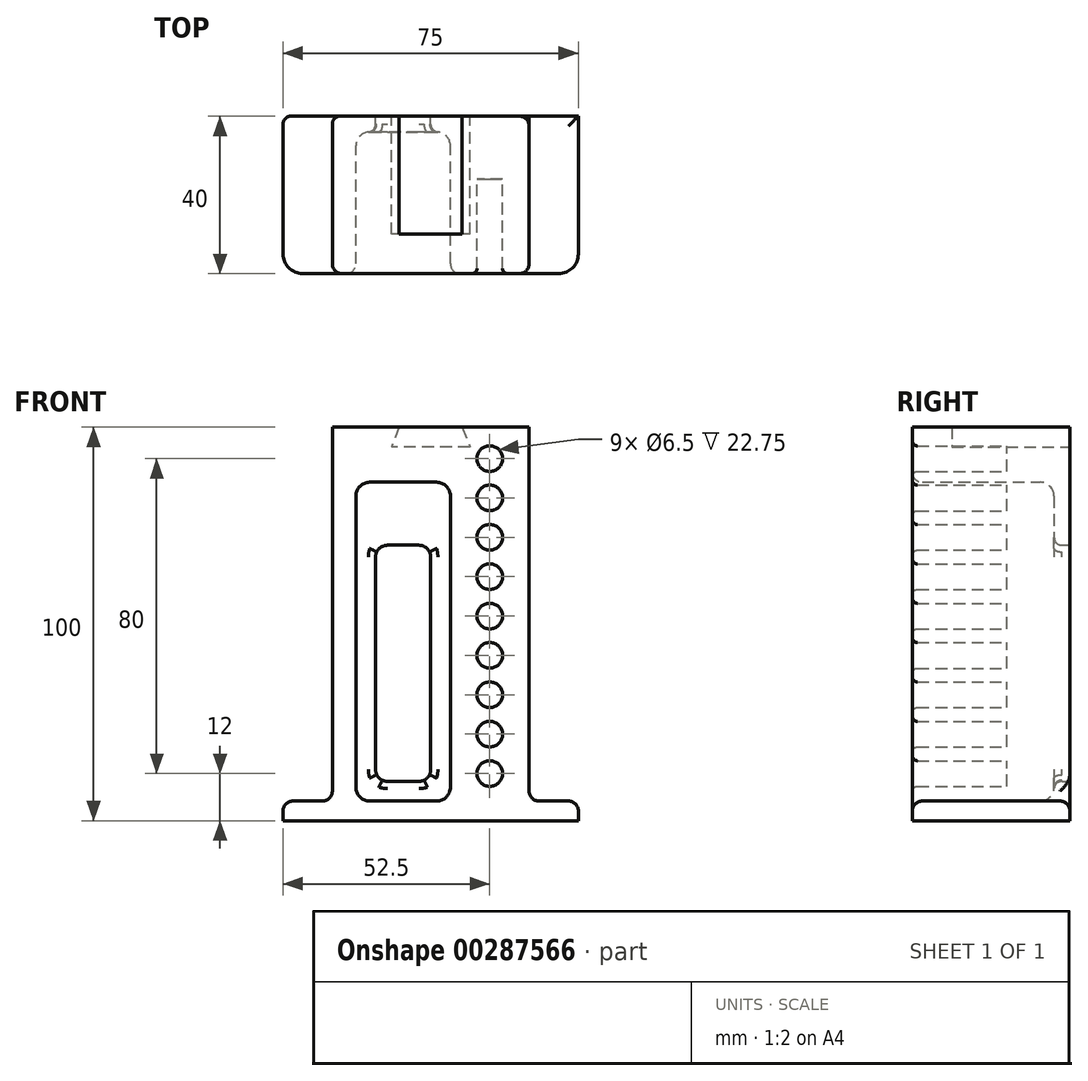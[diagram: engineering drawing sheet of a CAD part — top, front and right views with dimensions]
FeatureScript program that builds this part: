
annotation { "Feature Type Name" : "Feature", "Feature Type Description" : "" }
export const myFeature = defineFeature(function(context is Context, id is Id, definition is map)
    precondition{}
    {
        {
            var Q0;
            Q0=qCreatedBy(makeId("Front.planeOp"),FACE);
            var sketch = newSketch(context, id + "F0", { "sketchPlane" : qUnion([Q0])});
            skLineSegment(sketch, "E0", {"start": v(0, 0) * mm, "end": v(-25, 0) * mm});
            skLineSegment(sketch, "E1", {"start": v(-25, 0) * mm, "end": v(-25, -26.82) * mm});
            skLineSegment(sketch, "E2.bottom", {"start": v(-25, 0) * mm, "end": v(25, 0) * mm});
            skLineSegment(sketch, "E2.top", {"start": v(-25, 100) * mm, "end": v(25, 100) * mm});
            skLineSegment(sketch, "E2.left", {"start": v(-25, 0) * mm, "end": v(-25, 100) * mm});
            skLineSegment(sketch, "E2.right", {"start": v(25, 0) * mm, "end": v(25, 100) * mm});
            skSolve(sketch);
        }
        {
            var Q0;
            Q0=qSketchRegion(id+"F0",true);
            extrude(context, id + "F1", {"entities" : qUnion([Q0]), "endBound" : BoundingType.SYMMETRIC, "depth" : 40 * mm});
        }
        {
            var Q0;
            Q0=qCreatedBy(makeId("Top.planeOp"),FACE);
            var sketch = newSketch(context, id + "F2", { "sketchPlane" : qUnion([Q0])});
            skLineSegment(sketch, "E3.bottom", {"start": v(37.5, -20) * mm, "end": v(-37.5, -20) * mm});
            skLineSegment(sketch, "E3.top", {"start": v(37.5, 20) * mm, "end": v(-37.5, 20) * mm});
            skLineSegment(sketch, "E3.left", {"start": v(37.5, -20) * mm, "end": v(37.5, 20) * mm});
            skLineSegment(sketch, "E3.right", {"start": v(-37.5, -20) * mm, "end": v(-37.5, 20) * mm});
            skPoint(sketch, "E3.middle", {"position": v(0, 0) * mm});
            skSolve(sketch);
        }
        {
            var Q0;
            Q0=qSketchRegion(id+"F2",true);
            extrude(context, id + "F3", {"entities" : qUnion([Q0]), "operationType" : NewBodyOperationType.ADD, "depth" : 5 * mm});
        }
        {
            var Q0;
            Q0=qCreatedBy(makeId("Front.planeOp"),FACE);
            var sketch = newSketch(context, id + "F4", { "sketchPlane" : qUnion([Q0])});
            skLineSegment(sketch, "E4", {"start": v(0, 0) * mm, "end": v(0, 5) * mm});
            skLineSegment(sketch, "E5", {"start": v(0, 5) * mm, "end": v(-19, 5) * mm});
            skLineSegment(sketch, "E6", {"start": v(-19, 5) * mm, "end": v(-19, 86) * mm});
            skLineSegment(sketch, "E7", {"start": v(-19, 86) * mm, "end": v(5, 86) * mm});
            skLineSegment(sketch, "E8", {"start": v(5, 86) * mm, "end": v(5, 5) * mm});
            skLineSegment(sketch, "E9", {"start": v(5, 5) * mm, "end": v(0, 5) * mm});
            skSolve(sketch);
        }
        {
            var Q0;
            Q0=qSketchRegion(id+"F4",true);
            extrude(context, id + "F5", {"entities" : qUnion([Q0]), "endBound" : BoundingType.SYMMETRIC, "depth" : 48 * mm});
        }
        {
            var Q0;
            Q0=makeQuery(id+"F5.opExtrude","SWEPT_EDGE",EDGE,{"disambiguationData":[OSD([sQuery(id+"F4.wireOp",EDGE,"E6"),sQuery(id+"F4.wireOp",EDGE,"E7")])]});
            var Q1;
            Q1=makeQuery(id+"F5.opExtrude","SWEPT_EDGE",EDGE,{"disambiguationData":[OSD([sQuery(id+"F4.wireOp",EDGE,"E7"),sQuery(id+"F4.wireOp",EDGE,"E8")])]});
            var Q2;
            Q2=makeQuery(id+"F5.opExtrude","SWEPT_EDGE",EDGE,{"disambiguationData":[OSD([sQuery(id+"F4.wireOp",EDGE,"E5"),sQuery(id+"F4.wireOp",EDGE,"E6")])]});
            var Q3;
            Q3=makeQuery(id+"F5.opExtrude","SWEPT_EDGE",EDGE,{"disambiguationData":[OSD([sQuery(id+"F4.wireOp",EDGE,"E8"),sQuery(id+"F4.wireOp",EDGE,"E9")])]});
            var Q4;
            Q4=makeQuery(id+"F5.opExtrude","CAP_EDGE",EDGE,{"disambiguationData":[OSD([sQuery(id+"F4.wireOp",EDGE,"E7")])],"isStart":true});
            var Q5;
            Q5=makeQuery(id+"F5.opExtrude","CAP_EDGE",EDGE,{"disambiguationData":[OSD([sQuery(id+"F4.wireOp",EDGE,"E8")])],"isStart":true});
            var Q6;
            Q6=makeQuery(id+"F5.opExtrude","CAP_EDGE",EDGE,{"disambiguationData":[OSD([sQuery(id+"F4.wireOp",EDGE,"E6")])],"isStart":true});
            var Q7;
            Q7=makeQuery(id+"F5.opExtrude","CAP_EDGE",EDGE,{"disambiguationData":[OSD([sQuery(id+"F4.wireOp",EDGE,"E5"),sQuery(id+"F4.wireOp",EDGE,"E9")])],"isStart":true});
            fillet(context, id + "F6", {"entities" : qUnion([Q0, Q1, Q2, Q3, Q4, Q5, Q6, Q7]), "radius" : 3.5 * mm, "tangentPropagation" : true, "allowEdgeOverflow" : false});
        }
        {
            var Q0;
            Q0=makeQuery(id+"F5.opExtrude","SWEPT_BODY",BODY,{"disambiguationData":[OSD([sQuery(id+"F4.wireOp",EDGE,"E5"),sQuery(id+"F4.wireOp",EDGE,"E6"),sQuery(id+"F4.wireOp",EDGE,"E7"),sQuery(id+"F4.wireOp",EDGE,"E8"),sQuery(id+"F4.wireOp",EDGE,"E9")])]});
            transform(context, id + "F7", {"entities" : qUnion([Q0]), "transformType" : TransformType.TRANSLATION_3D, "dx" : 0 * mm, "dy" : -8 * mm, "dz" : 0 * mm, "makeCopy" : false});
        }
        {
            var Q0;
            Q0=makeQuery(id+"F5.opExtrude","SWEPT_BODY",BODY,{"disambiguationData":[OSD([sQuery(id+"F4.wireOp",EDGE,"E5"),sQuery(id+"F4.wireOp",EDGE,"E6"),sQuery(id+"F4.wireOp",EDGE,"E7"),sQuery(id+"F4.wireOp",EDGE,"E8"),sQuery(id+"F4.wireOp",EDGE,"E9")])]});
            transform(context, id + "F8", {"entities" : qUnion([Q0]), "transformType" : TransformType.COPY});
        }
        {
            var Q0;
            Q0=makeQuery(id+"F8.opPattern","COPY",BODY,{"derivedFrom":makeQuery(id+"F5.opExtrude","SWEPT_BODY",BODY,{"disambiguationData":[OSD([sQuery(id+"F4.wireOp",EDGE,"E5"),sQuery(id+"F4.wireOp",EDGE,"E6"),sQuery(id+"F4.wireOp",EDGE,"E7"),sQuery(id+"F4.wireOp",EDGE,"E8"),sQuery(id+"F4.wireOp",EDGE,"E9")])]}),"instanceName":"1"});
            var Q1;
            Q1=makeQuery(id+"F1.opExtrude","SWEPT_BODY",BODY,{"disambiguationData":[OSD([sQuery(id+"F0.wireOp",EDGE,"E2.bottom"),sQuery(id+"F0.wireOp",EDGE,"E2.top"),sQuery(id+"F0.wireOp",EDGE,"E2.left"),sQuery(id+"F0.wireOp",EDGE,"E2.right")])]});
            booleanBodies(context, id + "F9", {"operationType" : BooleanOperationType.SUBTRACTION, "tools" : qUnion([Q0]), "targets" : qUnion([Q1])});
        }
        {
            var Q0;
            {var subQ0=sQuery(id+"F2.wireOp",EDGE,"E3.bottom");var subQ2=sQuery(id+"F0.wireOp",EDGE,"E2.right");Q0=makeQuery(id+"F3.boolean.opBoolean","SPLIT",EDGE,{"disambiguationData":[TD([makeQuery(id+"F1.opExtrude","SWEPT_FACE",FACE,{"disambiguationData":[OSD([subQ2])]})])],"derivedFrom":makeQuery(id+"F3.opExtrude","CAP_EDGE",EDGE,{"disambiguationData":[OSD([subQ0])],"isStart":false})});}
            var Q1;
            Q1=makeQuery(id+"F3.opExtrude","CAP_EDGE",EDGE,{"disambiguationData":[OSD([sQuery(id+"F2.wireOp",EDGE,"E3.left")])],"isStart":false});
            var Q2;
            Q2=makeQuery(id+"F1.opExtrude","CAP_EDGE",EDGE,{"disambiguationData":[OSD([sQuery(id+"F0.wireOp",EDGE,"E2.right")])],"isStart":false});
            var Q3;
            {var subQ1=sQuery(id+"F2.wireOp",EDGE,"E3.top");var subQ2=sQuery(id+"F0.wireOp",EDGE,"E2.right");Q3=makeQuery(id+"F3.boolean.opBoolean","SPLIT",EDGE,{"disambiguationData":[TD([makeQuery(id+"F1.opExtrude","SWEPT_FACE",FACE,{"disambiguationData":[OSD([subQ2])]})])],"derivedFrom":makeQuery(id+"F3.opExtrude","CAP_EDGE",EDGE,{"disambiguationData":[OSD([subQ1])],"isStart":false})});}
            var Q4;
            {var subQ1=sQuery(id+"F2.wireOp",EDGE,"E3.bottom");var subQ2=sQuery(id+"F0.wireOp",EDGE,"E2.left");Q4=makeQuery(id+"F3.boolean.opBoolean","SPLIT",EDGE,{"disambiguationData":[TD([makeQuery(id+"F1.opExtrude","SWEPT_FACE",FACE,{"disambiguationData":[OSD([subQ2])]})])],"derivedFrom":makeQuery(id+"F3.opExtrude","CAP_EDGE",EDGE,{"disambiguationData":[OSD([subQ1])],"isStart":false})});}
            var Q5;
            Q5=makeQuery(id+"F3.opExtrude","CAP_EDGE",EDGE,{"disambiguationData":[OSD([sQuery(id+"F2.wireOp",EDGE,"E3.right")])],"isStart":false});
            var Q6;
            Q6=makeQuery(id+"F9.opBoolean","INTERSECT",EDGE,{"derivedFrom":[makeQuery(id+"F3.boolean.opBoolean","MERGE",FACE,{"derivedFrom":[makeQuery(id+"F1.opExtrude","CAP_FACE",FACE,{"disambiguationData":[OSD([sQuery(id+"F0.wireOp",EDGE,"E2.bottom"),sQuery(id+"F0.wireOp",EDGE,"E2.top"),sQuery(id+"F0.wireOp",EDGE,"E2.left"),sQuery(id+"F0.wireOp",EDGE,"E2.right")])],"isStart":false}),makeQuery(id+"F3.opExtrude","SWEPT_FACE",FACE,{"disambiguationData":[OSD([sQuery(id+"F2.wireOp",EDGE,"E3.bottom")])]})]}),makeQuery(id+"F8.opPattern","COPY",FACE,{"derivedFrom":makeQuery(id+"F5.opExtrude","SWEPT_FACE",FACE,{"disambiguationData":[OSD([sQuery(id+"F4.wireOp",EDGE,"E6")])]}),"instanceName":"1"})]});
            var Q7;
            Q7=makeQuery(id+"F1.opExtrude","CAP_EDGE",EDGE,{"disambiguationData":[OSD([sQuery(id+"F0.wireOp",EDGE,"E2.left")])],"isStart":false});
            var Q8;
            Q8=makeQuery(id+"F3.boolean.opBoolean","INTERSECT",EDGE,{"derivedFrom":[makeQuery(id+"F1.opExtrude","SWEPT_FACE",FACE,{"disambiguationData":[OSD([sQuery(id+"F0.wireOp",EDGE,"E2.left")])]}),makeQuery(id+"F3.opExtrude","CAP_FACE",FACE,{"disambiguationData":[OSD([sQuery(id+"F2.wireOp",EDGE,"E3.bottom"),sQuery(id+"F2.wireOp",EDGE,"E3.top"),sQuery(id+"F2.wireOp",EDGE,"E3.left"),sQuery(id+"F2.wireOp",EDGE,"E3.right")])],"isStart":false})]});
            var Q9;
            Q9=makeQuery(id+"F3.boolean.opBoolean","INTERSECT",EDGE,{"derivedFrom":[makeQuery(id+"F1.opExtrude","SWEPT_FACE",FACE,{"disambiguationData":[OSD([sQuery(id+"F0.wireOp",EDGE,"E2.right")])]}),makeQuery(id+"F3.opExtrude","CAP_FACE",FACE,{"disambiguationData":[OSD([sQuery(id+"F2.wireOp",EDGE,"E3.bottom"),sQuery(id+"F2.wireOp",EDGE,"E3.top"),sQuery(id+"F2.wireOp",EDGE,"E3.left"),sQuery(id+"F2.wireOp",EDGE,"E3.right")])],"isStart":false})]});
            fillet(context, id + "F10", {"entities" : qUnion([Q0, Q1, Q2, Q3, Q4, Q5, Q6, Q7, Q8, Q9]), "radius" : 2.5 * mm, "tangentPropagation" : true, "allowEdgeOverflow" : false});
        }
        {
            var Q0;
            Q0=makeQuery(id+"F3.opExtrude","SWEPT_EDGE",EDGE,{"disambiguationData":[OSD([sQuery(id+"F2.wireOp",EDGE,"E3.bottom"),sQuery(id+"F2.wireOp",EDGE,"E3.left")])]});
            var Q1;
            Q1=makeQuery(id+"F3.opExtrude","SWEPT_EDGE",EDGE,{"disambiguationData":[OSD([sQuery(id+"F2.wireOp",EDGE,"E3.bottom"),sQuery(id+"F2.wireOp",EDGE,"E3.right")])]});
            fillet(context, id + "F11", {"entities" : qUnion([Q0, Q1]), "radius" : 5 * mm, "tangentPropagation" : true, "allowEdgeOverflow" : false});
        }
        {
            var Q0;
            Q0=qCreatedBy(makeId("Front.planeOp"),FACE);
            var sketch = newSketch(context, id + "F12", { "sketchPlane" : qUnion([Q0])});
            skLineSegment(sketch, "E10", {"start": v(0, 0) * mm, "end": v(0, 40) * mm});
            skLineSegment(sketch, "E11", {"start": v(-7, 70) * mm, "end": v(0, 70) * mm});
            skLineSegment(sketch, "E12", {"start": v(0, 70) * mm, "end": v(0, 40) * mm});
            skLineSegment(sketch, "E13", {"start": v(-7, 70) * mm, "end": v(-14, 70) * mm});
            skLineSegment(sketch, "E14", {"start": v(-14, 70) * mm, "end": v(-14, 10) * mm});
            skLineSegment(sketch, "E15", {"start": v(-14, 10) * mm, "end": v(0, 10) * mm});
            skLineSegment(sketch, "E16", {"start": v(0, 10) * mm, "end": v(0, 40) * mm});
            skSolve(sketch);
        }
        {
            var Q0;
            Q0=qSketchRegion(id+"F12",true);
            extrude(context, id + "F13", {"entities" : qUnion([Q0]), "endBound" : BoundingType.SYMMETRIC, "depth" : 50 * mm});
        }
        {
            var Q0;
            Q0=makeQuery(id+"F13.opExtrude","SWEPT_EDGE",EDGE,{"disambiguationData":[OSD([sQuery(id+"F12.wireOp",EDGE,"E13"),sQuery(id+"F12.wireOp",EDGE,"E14")])]});
            var Q1;
            Q1=makeQuery(id+"F13.opExtrude","SWEPT_EDGE",EDGE,{"disambiguationData":[OSD([sQuery(id+"F12.wireOp",EDGE,"E11"),sQuery(id+"F12.wireOp",EDGE,"E12")])]});
            var Q2;
            Q2=makeQuery(id+"F13.opExtrude","SWEPT_EDGE",EDGE,{"disambiguationData":[OSD([sQuery(id+"F12.wireOp",EDGE,"E14"),sQuery(id+"F12.wireOp",EDGE,"E15")])]});
            var Q3;
            Q3=makeQuery(id+"F13.opExtrude","SWEPT_EDGE",EDGE,{"disambiguationData":[OSD([sQuery(id+"F12.wireOp",EDGE,"E15"),sQuery(id+"F12.wireOp",EDGE,"E16")])]});
            fillet(context, id + "F14", {"entities" : qUnion([Q0, Q1, Q2, Q3]), "radius" : 3 * mm, "tangentPropagation" : true, "allowEdgeOverflow" : false});
        }
        {
            var Q0;
            Q0=makeQuery(id+"F13.opExtrude","SWEPT_BODY",BODY,{"disambiguationData":[OSD([sQuery(id+"F12.wireOp",EDGE,"E11"),sQuery(id+"F12.wireOp",EDGE,"E12"),sQuery(id+"F12.wireOp",EDGE,"E13"),sQuery(id+"F12.wireOp",EDGE,"E14"),sQuery(id+"F12.wireOp",EDGE,"E15"),sQuery(id+"F12.wireOp",EDGE,"E16")])]});
            var Q1;
            Q1=makeQuery(id+"F1.opExtrude","SWEPT_BODY",BODY,{"disambiguationData":[OSD([sQuery(id+"F0.wireOp",EDGE,"E2.bottom"),sQuery(id+"F0.wireOp",EDGE,"E2.top"),sQuery(id+"F0.wireOp",EDGE,"E2.left"),sQuery(id+"F0.wireOp",EDGE,"E2.right")])]});
            booleanBodies(context, id + "F15", {"operationType" : BooleanOperationType.SUBTRACTION, "tools" : qUnion([Q0]), "targets" : qUnion([Q1])});
        }
        {
            var Q0;
            Q0=qCreatedBy(makeId("Front.planeOp"),FACE);
            var sketch = newSketch(context, id + "F16", { "sketchPlane" : qUnion([Q0])});
            skCircle(sketch, "E17", {"center": v(15, 12) * mm, "radius": 3.25 * mm});
            skSolve(sketch);
        }
        {
            var Q0;
            Q0=qSketchRegion(id+"F16",true);
            extrude(context, id + "F17", {"entities" : qUnion([Q0]), "depth" : 25 * mm});
        }
        {
            var Q0;
            Q0=makeQuery(id+"F17.opExtrude","SWEPT_BODY",BODY,{"disambiguationData":[OSD([sQuery(id+"F16.wireOp",EDGE,"E17")])]});
            transform(context, id + "F18", {"entities" : qUnion([Q0]), "transformType" : TransformType.TRANSLATION_3D, "dx" : 0 * mm, "dy" : 4 * mm, "dz" : 0 * mm, "makeCopy" : false});
        }
        {
            var Q0;
            Q0=makeQuery(id+"F17.opExtrude","SWEPT_BODY",BODY,{"disambiguationData":[OSD([sQuery(id+"F16.wireOp",EDGE,"E17")])]});
            transform(context, id + "F19", {"entities" : qUnion([Q0]), "transformType" : TransformType.COPY});
        }
        {
            var Q0;
            Q0=makeQuery(id+"F19.opPattern","COPY",BODY,{"derivedFrom":makeQuery(id+"F17.opExtrude","SWEPT_BODY",BODY,{"disambiguationData":[OSD([sQuery(id+"F16.wireOp",EDGE,"E17")])]}),"instanceName":"1"});
            transform(context, id + "F20", {"entities" : qUnion([Q0]), "transformType" : TransformType.COPY});
        }
        {
            var Q0;
            Q0=makeQuery(id+"F20.opPattern","COPY",BODY,{"derivedFrom":makeQuery(id+"F19.opPattern","COPY",BODY,{"derivedFrom":makeQuery(id+"F17.opExtrude","SWEPT_BODY",BODY,{"disambiguationData":[OSD([sQuery(id+"F16.wireOp",EDGE,"E17")])]}),"instanceName":"1"}),"instanceName":"1"});
            transform(context, id + "F21", {"entities" : qUnion([Q0]), "transformType" : TransformType.COPY});
        }
        {
            var Q0;
            Q0=makeQuery(id+"F21.opPattern","COPY",BODY,{"derivedFrom":makeQuery(id+"F20.opPattern","COPY",BODY,{"derivedFrom":makeQuery(id+"F19.opPattern","COPY",BODY,{"derivedFrom":makeQuery(id+"F17.opExtrude","SWEPT_BODY",BODY,{"disambiguationData":[OSD([sQuery(id+"F16.wireOp",EDGE,"E17")])]}),"instanceName":"1"}),"instanceName":"1"}),"instanceName":"1"});
            transform(context, id + "F22", {"entities" : qUnion([Q0]), "transformType" : TransformType.COPY});
        }
        {
            var Q0;
            Q0=makeQuery(id+"F19.opPattern","COPY",BODY,{"derivedFrom":makeQuery(id+"F17.opExtrude","SWEPT_BODY",BODY,{"disambiguationData":[OSD([sQuery(id+"F16.wireOp",EDGE,"E17")])]}),"instanceName":"1"});
            transform(context, id + "F23", {"entities" : qUnion([Q0]), "transformType" : TransformType.TRANSLATION_3D, "dx" : 0 * mm, "dy" : 0 * mm, "dz" : 10 * mm, "makeCopy" : false});
        }
        {
            var Q0;
            Q0=makeQuery(id+"F20.opPattern","COPY",BODY,{"derivedFrom":makeQuery(id+"F19.opPattern","COPY",BODY,{"derivedFrom":makeQuery(id+"F17.opExtrude","SWEPT_BODY",BODY,{"disambiguationData":[OSD([sQuery(id+"F16.wireOp",EDGE,"E17")])]}),"instanceName":"1"}),"instanceName":"1"});
            transform(context, id + "F24", {"entities" : qUnion([Q0]), "transformType" : TransformType.TRANSLATION_3D, "dx" : 0 * mm, "dy" : 0 * mm, "dz" : 20 * mm, "makeCopy" : false});
        }
        {
            var Q0;
            Q0=makeQuery(id+"F21.opPattern","COPY",BODY,{"derivedFrom":makeQuery(id+"F20.opPattern","COPY",BODY,{"derivedFrom":makeQuery(id+"F19.opPattern","COPY",BODY,{"derivedFrom":makeQuery(id+"F17.opExtrude","SWEPT_BODY",BODY,{"disambiguationData":[OSD([sQuery(id+"F16.wireOp",EDGE,"E17")])]}),"instanceName":"1"}),"instanceName":"1"}),"instanceName":"1"});
            transform(context, id + "F25", {"entities" : qUnion([Q0]), "transformType" : TransformType.TRANSLATION_3D, "dx" : 0 * mm, "dy" : 0 * mm, "dz" : 30 * mm, "makeCopy" : false});
        }
        {
            var Q0;
            Q0=makeQuery(id+"F22.opPattern","COPY",BODY,{"derivedFrom":makeQuery(id+"F21.opPattern","COPY",BODY,{"derivedFrom":makeQuery(id+"F20.opPattern","COPY",BODY,{"derivedFrom":makeQuery(id+"F19.opPattern","COPY",BODY,{"derivedFrom":makeQuery(id+"F17.opExtrude","SWEPT_BODY",BODY,{"disambiguationData":[OSD([sQuery(id+"F16.wireOp",EDGE,"E17")])]}),"instanceName":"1"}),"instanceName":"1"}),"instanceName":"1"}),"instanceName":"1"});
            transform(context, id + "F26", {"entities" : qUnion([Q0]), "transformType" : TransformType.TRANSLATION_3D, "dx" : 0 * mm, "dy" : 0 * mm, "dz" : 40 * mm, "makeCopy" : false});
        }
        {
            var Q0;
            Q0=makeQuery(id+"F22.opPattern","COPY",BODY,{"derivedFrom":makeQuery(id+"F21.opPattern","COPY",BODY,{"derivedFrom":makeQuery(id+"F20.opPattern","COPY",BODY,{"derivedFrom":makeQuery(id+"F19.opPattern","COPY",BODY,{"derivedFrom":makeQuery(id+"F17.opExtrude","SWEPT_BODY",BODY,{"disambiguationData":[OSD([sQuery(id+"F16.wireOp",EDGE,"E17")])]}),"instanceName":"1"}),"instanceName":"1"}),"instanceName":"1"}),"instanceName":"1"});
            var Q1;
            Q1=makeQuery(id+"F21.opPattern","COPY",BODY,{"derivedFrom":makeQuery(id+"F20.opPattern","COPY",BODY,{"derivedFrom":makeQuery(id+"F19.opPattern","COPY",BODY,{"derivedFrom":makeQuery(id+"F17.opExtrude","SWEPT_BODY",BODY,{"disambiguationData":[OSD([sQuery(id+"F16.wireOp",EDGE,"E17")])]}),"instanceName":"1"}),"instanceName":"1"}),"instanceName":"1"});
            var Q2;
            Q2=makeQuery(id+"F20.opPattern","COPY",BODY,{"derivedFrom":makeQuery(id+"F19.opPattern","COPY",BODY,{"derivedFrom":makeQuery(id+"F17.opExtrude","SWEPT_BODY",BODY,{"disambiguationData":[OSD([sQuery(id+"F16.wireOp",EDGE,"E17")])]}),"instanceName":"1"}),"instanceName":"1"});
            var Q3;
            Q3=makeQuery(id+"F19.opPattern","COPY",BODY,{"derivedFrom":makeQuery(id+"F17.opExtrude","SWEPT_BODY",BODY,{"disambiguationData":[OSD([sQuery(id+"F16.wireOp",EDGE,"E17")])]}),"instanceName":"1"});
            transform(context, id + "F27", {"entities" : qUnion([Q0, Q1, Q2, Q3]), "transformType" : TransformType.COPY});
        }
        {
            var Q0;
            Q0=makeQuery(id+"F27.opPattern","COPY",BODY,{"derivedFrom":makeQuery(id+"F19.opPattern","COPY",BODY,{"derivedFrom":makeQuery(id+"F17.opExtrude","SWEPT_BODY",BODY,{"disambiguationData":[OSD([sQuery(id+"F16.wireOp",EDGE,"E17")])]}),"instanceName":"1"}),"instanceName":"1"});
            var Q1;
            Q1=makeQuery(id+"F27.opPattern","COPY",BODY,{"derivedFrom":makeQuery(id+"F20.opPattern","COPY",BODY,{"derivedFrom":makeQuery(id+"F19.opPattern","COPY",BODY,{"derivedFrom":makeQuery(id+"F17.opExtrude","SWEPT_BODY",BODY,{"disambiguationData":[OSD([sQuery(id+"F16.wireOp",EDGE,"E17")])]}),"instanceName":"1"}),"instanceName":"1"}),"instanceName":"1"});
            var Q2;
            Q2=makeQuery(id+"F27.opPattern","COPY",BODY,{"derivedFrom":makeQuery(id+"F21.opPattern","COPY",BODY,{"derivedFrom":makeQuery(id+"F20.opPattern","COPY",BODY,{"derivedFrom":makeQuery(id+"F19.opPattern","COPY",BODY,{"derivedFrom":makeQuery(id+"F17.opExtrude","SWEPT_BODY",BODY,{"disambiguationData":[OSD([sQuery(id+"F16.wireOp",EDGE,"E17")])]}),"instanceName":"1"}),"instanceName":"1"}),"instanceName":"1"}),"instanceName":"1"});
            var Q3;
            Q3=makeQuery(id+"F27.opPattern","COPY",BODY,{"derivedFrom":makeQuery(id+"F22.opPattern","COPY",BODY,{"derivedFrom":makeQuery(id+"F21.opPattern","COPY",BODY,{"derivedFrom":makeQuery(id+"F20.opPattern","COPY",BODY,{"derivedFrom":makeQuery(id+"F19.opPattern","COPY",BODY,{"derivedFrom":makeQuery(id+"F17.opExtrude","SWEPT_BODY",BODY,{"disambiguationData":[OSD([sQuery(id+"F16.wireOp",EDGE,"E17")])]}),"instanceName":"1"}),"instanceName":"1"}),"instanceName":"1"}),"instanceName":"1"}),"instanceName":"1"});
            transform(context, id + "F28", {"entities" : qUnion([Q0, Q1, Q2, Q3]), "transformType" : TransformType.TRANSLATION_3D, "dx" : 0 * mm, "dy" : 0 * mm, "dz" : 40 * mm, "makeCopy" : false});
        }
        {
            var Q0;
            Q0=makeQuery(id+"F17.opExtrude","SWEPT_BODY",BODY,{"disambiguationData":[OSD([sQuery(id+"F16.wireOp",EDGE,"E17")])]});
            var Q1;
            Q1=makeQuery(id+"F19.opPattern","COPY",BODY,{"derivedFrom":makeQuery(id+"F17.opExtrude","SWEPT_BODY",BODY,{"disambiguationData":[OSD([sQuery(id+"F16.wireOp",EDGE,"E17")])]}),"instanceName":"1"});
            var Q2;
            Q2=makeQuery(id+"F20.opPattern","COPY",BODY,{"derivedFrom":makeQuery(id+"F19.opPattern","COPY",BODY,{"derivedFrom":makeQuery(id+"F17.opExtrude","SWEPT_BODY",BODY,{"disambiguationData":[OSD([sQuery(id+"F16.wireOp",EDGE,"E17")])]}),"instanceName":"1"}),"instanceName":"1"});
            var Q3;
            Q3=makeQuery(id+"F21.opPattern","COPY",BODY,{"derivedFrom":makeQuery(id+"F20.opPattern","COPY",BODY,{"derivedFrom":makeQuery(id+"F19.opPattern","COPY",BODY,{"derivedFrom":makeQuery(id+"F17.opExtrude","SWEPT_BODY",BODY,{"disambiguationData":[OSD([sQuery(id+"F16.wireOp",EDGE,"E17")])]}),"instanceName":"1"}),"instanceName":"1"}),"instanceName":"1"});
            var Q4;
            Q4=makeQuery(id+"F22.opPattern","COPY",BODY,{"derivedFrom":makeQuery(id+"F21.opPattern","COPY",BODY,{"derivedFrom":makeQuery(id+"F20.opPattern","COPY",BODY,{"derivedFrom":makeQuery(id+"F19.opPattern","COPY",BODY,{"derivedFrom":makeQuery(id+"F17.opExtrude","SWEPT_BODY",BODY,{"disambiguationData":[OSD([sQuery(id+"F16.wireOp",EDGE,"E17")])]}),"instanceName":"1"}),"instanceName":"1"}),"instanceName":"1"}),"instanceName":"1"});
            var Q5;
            Q5=makeQuery(id+"F27.opPattern","COPY",BODY,{"derivedFrom":makeQuery(id+"F19.opPattern","COPY",BODY,{"derivedFrom":makeQuery(id+"F17.opExtrude","SWEPT_BODY",BODY,{"disambiguationData":[OSD([sQuery(id+"F16.wireOp",EDGE,"E17")])]}),"instanceName":"1"}),"instanceName":"1"});
            var Q6;
            Q6=makeQuery(id+"F27.opPattern","COPY",BODY,{"derivedFrom":makeQuery(id+"F20.opPattern","COPY",BODY,{"derivedFrom":makeQuery(id+"F19.opPattern","COPY",BODY,{"derivedFrom":makeQuery(id+"F17.opExtrude","SWEPT_BODY",BODY,{"disambiguationData":[OSD([sQuery(id+"F16.wireOp",EDGE,"E17")])]}),"instanceName":"1"}),"instanceName":"1"}),"instanceName":"1"});
            var Q7;
            Q7=makeQuery(id+"F27.opPattern","COPY",BODY,{"derivedFrom":makeQuery(id+"F21.opPattern","COPY",BODY,{"derivedFrom":makeQuery(id+"F20.opPattern","COPY",BODY,{"derivedFrom":makeQuery(id+"F19.opPattern","COPY",BODY,{"derivedFrom":makeQuery(id+"F17.opExtrude","SWEPT_BODY",BODY,{"disambiguationData":[OSD([sQuery(id+"F16.wireOp",EDGE,"E17")])]}),"instanceName":"1"}),"instanceName":"1"}),"instanceName":"1"}),"instanceName":"1"});
            var Q8;
            Q8=makeQuery(id+"F27.opPattern","COPY",BODY,{"derivedFrom":makeQuery(id+"F22.opPattern","COPY",BODY,{"derivedFrom":makeQuery(id+"F21.opPattern","COPY",BODY,{"derivedFrom":makeQuery(id+"F20.opPattern","COPY",BODY,{"derivedFrom":makeQuery(id+"F19.opPattern","COPY",BODY,{"derivedFrom":makeQuery(id+"F17.opExtrude","SWEPT_BODY",BODY,{"disambiguationData":[OSD([sQuery(id+"F16.wireOp",EDGE,"E17")])]}),"instanceName":"1"}),"instanceName":"1"}),"instanceName":"1"}),"instanceName":"1"}),"instanceName":"1"});
            var Q9;
            Q9=makeQuery(id+"F1.opExtrude","SWEPT_BODY",BODY,{"disambiguationData":[OSD([sQuery(id+"F0.wireOp",EDGE,"E2.bottom"),sQuery(id+"F0.wireOp",EDGE,"E2.top"),sQuery(id+"F0.wireOp",EDGE,"E2.left"),sQuery(id+"F0.wireOp",EDGE,"E2.right")])]});
            booleanBodies(context, id + "F29", {"operationType" : BooleanOperationType.SUBTRACTION, "tools" : qUnion([Q0, Q1, Q2, Q3, Q4, Q5, Q6, Q7, Q8]), "targets" : qUnion([Q9])});
        }
        {
            var Q0;
            Q0=makeQuery(id+"F29.opBoolean","INTERSECT",EDGE,{"derivedFrom":[makeQuery(id+"F3.boolean.opBoolean","MERGE",FACE,{"derivedFrom":[makeQuery(id+"F1.opExtrude","CAP_FACE",FACE,{"disambiguationData":[OSD([sQuery(id+"F0.wireOp",EDGE,"E2.bottom"),sQuery(id+"F0.wireOp",EDGE,"E2.top"),sQuery(id+"F0.wireOp",EDGE,"E2.left"),sQuery(id+"F0.wireOp",EDGE,"E2.right")])],"isStart":false}),makeQuery(id+"F3.opExtrude","SWEPT_FACE",FACE,{"disambiguationData":[OSD([sQuery(id+"F2.wireOp",EDGE,"E3.bottom")])]})]}),makeQuery(id+"F17.opExtrude","SWEPT_FACE",FACE,{"disambiguationData":[OSD([sQuery(id+"F16.wireOp",EDGE,"E17")])]})]});
            var Q1;
            Q1=makeQuery(id+"F29.opBoolean","INTERSECT",EDGE,{"derivedFrom":[makeQuery(id+"F3.boolean.opBoolean","MERGE",FACE,{"derivedFrom":[makeQuery(id+"F1.opExtrude","CAP_FACE",FACE,{"disambiguationData":[OSD([sQuery(id+"F0.wireOp",EDGE,"E2.bottom"),sQuery(id+"F0.wireOp",EDGE,"E2.top"),sQuery(id+"F0.wireOp",EDGE,"E2.left"),sQuery(id+"F0.wireOp",EDGE,"E2.right")])],"isStart":false}),makeQuery(id+"F3.opExtrude","SWEPT_FACE",FACE,{"disambiguationData":[OSD([sQuery(id+"F2.wireOp",EDGE,"E3.bottom")])]})]}),makeQuery(id+"F19.opPattern","COPY",FACE,{"derivedFrom":makeQuery(id+"F17.opExtrude","SWEPT_FACE",FACE,{"disambiguationData":[OSD([sQuery(id+"F16.wireOp",EDGE,"E17")])]}),"instanceName":"1"})]});
            var Q2;
            Q2=makeQuery(id+"F29.opBoolean","INTERSECT",EDGE,{"derivedFrom":[makeQuery(id+"F3.boolean.opBoolean","MERGE",FACE,{"derivedFrom":[makeQuery(id+"F1.opExtrude","CAP_FACE",FACE,{"disambiguationData":[OSD([sQuery(id+"F0.wireOp",EDGE,"E2.bottom"),sQuery(id+"F0.wireOp",EDGE,"E2.top"),sQuery(id+"F0.wireOp",EDGE,"E2.left"),sQuery(id+"F0.wireOp",EDGE,"E2.right")])],"isStart":false}),makeQuery(id+"F3.opExtrude","SWEPT_FACE",FACE,{"disambiguationData":[OSD([sQuery(id+"F2.wireOp",EDGE,"E3.bottom")])]})]}),makeQuery(id+"F20.opPattern","COPY",FACE,{"derivedFrom":makeQuery(id+"F19.opPattern","COPY",FACE,{"derivedFrom":makeQuery(id+"F17.opExtrude","SWEPT_FACE",FACE,{"disambiguationData":[OSD([sQuery(id+"F16.wireOp",EDGE,"E17")])]}),"instanceName":"1"}),"instanceName":"1"})]});
            var Q3;
            Q3=makeQuery(id+"F29.opBoolean","INTERSECT",EDGE,{"derivedFrom":[makeQuery(id+"F3.boolean.opBoolean","MERGE",FACE,{"derivedFrom":[makeQuery(id+"F1.opExtrude","CAP_FACE",FACE,{"disambiguationData":[OSD([sQuery(id+"F0.wireOp",EDGE,"E2.bottom"),sQuery(id+"F0.wireOp",EDGE,"E2.top"),sQuery(id+"F0.wireOp",EDGE,"E2.left"),sQuery(id+"F0.wireOp",EDGE,"E2.right")])],"isStart":false}),makeQuery(id+"F3.opExtrude","SWEPT_FACE",FACE,{"disambiguationData":[OSD([sQuery(id+"F2.wireOp",EDGE,"E3.bottom")])]})]}),makeQuery(id+"F21.opPattern","COPY",FACE,{"derivedFrom":makeQuery(id+"F20.opPattern","COPY",FACE,{"derivedFrom":makeQuery(id+"F19.opPattern","COPY",FACE,{"derivedFrom":makeQuery(id+"F17.opExtrude","SWEPT_FACE",FACE,{"disambiguationData":[OSD([sQuery(id+"F16.wireOp",EDGE,"E17")])]}),"instanceName":"1"}),"instanceName":"1"}),"instanceName":"1"})]});
            var Q4;
            Q4=makeQuery(id+"F29.opBoolean","INTERSECT",EDGE,{"derivedFrom":[makeQuery(id+"F3.boolean.opBoolean","MERGE",FACE,{"derivedFrom":[makeQuery(id+"F1.opExtrude","CAP_FACE",FACE,{"disambiguationData":[OSD([sQuery(id+"F0.wireOp",EDGE,"E2.bottom"),sQuery(id+"F0.wireOp",EDGE,"E2.top"),sQuery(id+"F0.wireOp",EDGE,"E2.left"),sQuery(id+"F0.wireOp",EDGE,"E2.right")])],"isStart":false}),makeQuery(id+"F3.opExtrude","SWEPT_FACE",FACE,{"disambiguationData":[OSD([sQuery(id+"F2.wireOp",EDGE,"E3.bottom")])]})]}),makeQuery(id+"F22.opPattern","COPY",FACE,{"derivedFrom":makeQuery(id+"F21.opPattern","COPY",FACE,{"derivedFrom":makeQuery(id+"F20.opPattern","COPY",FACE,{"derivedFrom":makeQuery(id+"F19.opPattern","COPY",FACE,{"derivedFrom":makeQuery(id+"F17.opExtrude","SWEPT_FACE",FACE,{"disambiguationData":[OSD([sQuery(id+"F16.wireOp",EDGE,"E17")])]}),"instanceName":"1"}),"instanceName":"1"}),"instanceName":"1"}),"instanceName":"1"})]});
            var Q5;
            Q5=makeQuery(id+"F29.opBoolean","INTERSECT",EDGE,{"derivedFrom":[makeQuery(id+"F3.boolean.opBoolean","MERGE",FACE,{"derivedFrom":[makeQuery(id+"F1.opExtrude","CAP_FACE",FACE,{"disambiguationData":[OSD([sQuery(id+"F0.wireOp",EDGE,"E2.bottom"),sQuery(id+"F0.wireOp",EDGE,"E2.top"),sQuery(id+"F0.wireOp",EDGE,"E2.left"),sQuery(id+"F0.wireOp",EDGE,"E2.right")])],"isStart":false}),makeQuery(id+"F3.opExtrude","SWEPT_FACE",FACE,{"disambiguationData":[OSD([sQuery(id+"F2.wireOp",EDGE,"E3.bottom")])]})]}),makeQuery(id+"F27.opPattern","COPY",FACE,{"derivedFrom":makeQuery(id+"F19.opPattern","COPY",FACE,{"derivedFrom":makeQuery(id+"F17.opExtrude","SWEPT_FACE",FACE,{"disambiguationData":[OSD([sQuery(id+"F16.wireOp",EDGE,"E17")])]}),"instanceName":"1"}),"instanceName":"1"})]});
            var Q6;
            Q6=makeQuery(id+"F29.opBoolean","INTERSECT",EDGE,{"derivedFrom":[makeQuery(id+"F3.boolean.opBoolean","MERGE",FACE,{"derivedFrom":[makeQuery(id+"F1.opExtrude","CAP_FACE",FACE,{"disambiguationData":[OSD([sQuery(id+"F0.wireOp",EDGE,"E2.bottom"),sQuery(id+"F0.wireOp",EDGE,"E2.top"),sQuery(id+"F0.wireOp",EDGE,"E2.left"),sQuery(id+"F0.wireOp",EDGE,"E2.right")])],"isStart":false}),makeQuery(id+"F3.opExtrude","SWEPT_FACE",FACE,{"disambiguationData":[OSD([sQuery(id+"F2.wireOp",EDGE,"E3.bottom")])]})]}),makeQuery(id+"F27.opPattern","COPY",FACE,{"derivedFrom":makeQuery(id+"F20.opPattern","COPY",FACE,{"derivedFrom":makeQuery(id+"F19.opPattern","COPY",FACE,{"derivedFrom":makeQuery(id+"F17.opExtrude","SWEPT_FACE",FACE,{"disambiguationData":[OSD([sQuery(id+"F16.wireOp",EDGE,"E17")])]}),"instanceName":"1"}),"instanceName":"1"}),"instanceName":"1"})]});
            var Q7;
            Q7=makeQuery(id+"F29.opBoolean","INTERSECT",EDGE,{"derivedFrom":[makeQuery(id+"F3.boolean.opBoolean","MERGE",FACE,{"derivedFrom":[makeQuery(id+"F1.opExtrude","CAP_FACE",FACE,{"disambiguationData":[OSD([sQuery(id+"F0.wireOp",EDGE,"E2.bottom"),sQuery(id+"F0.wireOp",EDGE,"E2.top"),sQuery(id+"F0.wireOp",EDGE,"E2.left"),sQuery(id+"F0.wireOp",EDGE,"E2.right")])],"isStart":false}),makeQuery(id+"F3.opExtrude","SWEPT_FACE",FACE,{"disambiguationData":[OSD([sQuery(id+"F2.wireOp",EDGE,"E3.bottom")])]})]}),makeQuery(id+"F27.opPattern","COPY",FACE,{"derivedFrom":makeQuery(id+"F21.opPattern","COPY",FACE,{"derivedFrom":makeQuery(id+"F20.opPattern","COPY",FACE,{"derivedFrom":makeQuery(id+"F19.opPattern","COPY",FACE,{"derivedFrom":makeQuery(id+"F17.opExtrude","SWEPT_FACE",FACE,{"disambiguationData":[OSD([sQuery(id+"F16.wireOp",EDGE,"E17")])]}),"instanceName":"1"}),"instanceName":"1"}),"instanceName":"1"}),"instanceName":"1"})]});
            var Q8;
            Q8=makeQuery(id+"F29.opBoolean","INTERSECT",EDGE,{"derivedFrom":[makeQuery(id+"F3.boolean.opBoolean","MERGE",FACE,{"derivedFrom":[makeQuery(id+"F1.opExtrude","CAP_FACE",FACE,{"disambiguationData":[OSD([sQuery(id+"F0.wireOp",EDGE,"E2.bottom"),sQuery(id+"F0.wireOp",EDGE,"E2.top"),sQuery(id+"F0.wireOp",EDGE,"E2.left"),sQuery(id+"F0.wireOp",EDGE,"E2.right")])],"isStart":false}),makeQuery(id+"F3.opExtrude","SWEPT_FACE",FACE,{"disambiguationData":[OSD([sQuery(id+"F2.wireOp",EDGE,"E3.bottom")])]})]}),makeQuery(id+"F27.opPattern","COPY",FACE,{"derivedFrom":makeQuery(id+"F22.opPattern","COPY",FACE,{"derivedFrom":makeQuery(id+"F21.opPattern","COPY",FACE,{"derivedFrom":makeQuery(id+"F20.opPattern","COPY",FACE,{"derivedFrom":makeQuery(id+"F19.opPattern","COPY",FACE,{"derivedFrom":makeQuery(id+"F17.opExtrude","SWEPT_FACE",FACE,{"disambiguationData":[OSD([sQuery(id+"F16.wireOp",EDGE,"E17")])]}),"instanceName":"1"}),"instanceName":"1"}),"instanceName":"1"}),"instanceName":"1"}),"instanceName":"1"})]});
            fillet(context, id + "F30", {"entities" : qUnion([Q0, Q1, Q2, Q3, Q4, Q5, Q6, Q7, Q8]), "radius" : 1.25 * mm, "tangentPropagation" : true, "allowEdgeOverflow" : false});
        }
        {
            var Q0;
            Q0=makeQuery(id+"F1.opExtrude","CAP_EDGE",EDGE,{"disambiguationData":[OSD([sQuery(id+"F0.wireOp",EDGE,"E2.left")])],"isStart":true});
            var Q1;
            Q1=makeQuery(id+"F15.opBoolean","INTERSECT",EDGE,{"derivedFrom":[makeQuery(id+"F9.opBoolean","COPY",FACE,{"derivedFrom":makeQuery(id+"F8.opPattern","COPY",FACE,{"derivedFrom":makeQuery(id+"F5.opExtrude","CAP_FACE",FACE,{"disambiguationData":[OSD([sQuery(id+"F4.wireOp",EDGE,"E5"),sQuery(id+"F4.wireOp",EDGE,"E6"),sQuery(id+"F4.wireOp",EDGE,"E7"),sQuery(id+"F4.wireOp",EDGE,"E8"),sQuery(id+"F4.wireOp",EDGE,"E9")])],"isStart":true}),"instanceName":"1"})}),makeQuery(id+"F13.opExtrude","SWEPT_FACE",FACE,{"disambiguationData":[OSD([sQuery(id+"F12.wireOp",EDGE,"E11"),sQuery(id+"F12.wireOp",EDGE,"E13")])]})]});
            fillet(context, id + "F31", {"entities" : qUnion([Q0, Q1]), "radius" : 2 * mm, "tangentPropagation" : true, "allowEdgeOverflow" : false});
        }
        {
            var Q0;
            Q0=qCreatedBy(makeId("Front.planeOp"),FACE);
            var sketch = newSketch(context, id + "F32", { "sketchPlane" : qUnion([Q0])});
            skLineSegment(sketch, "E18", {"start": v(0, 95) * mm, "end": v(10, 95) * mm});
            skLineSegment(sketch, "E19", {"start": v(0, 95) * mm, "end": v(-10, 95) * mm});
            skLineSegment(sketch, "E20", {"start": v(0, 100) * mm, "end": v(-8, 100) * mm});
            skLineSegment(sketch, "E21", {"start": v(-8, 100) * mm, "end": v(-10, 95) * mm});
            skLineSegment(sketch, "E22", {"start": v(0, 100) * mm, "end": v(8, 100) * mm});
            skLineSegment(sketch, "E23", {"start": v(8, 100) * mm, "end": v(10, 95) * mm});
            skSolve(sketch);
        }
        {
            var Q0;
            Q0=qSketchRegion(id+"F32",true);
            extrude(context, id + "F33", {"entities" : qUnion([Q0]), "endBound" : BoundingType.SYMMETRIC, "depth" : 30 * mm});
        }
        {
            var Q0;
            Q0=makeQuery(id+"F33.opExtrude","SWEPT_BODY",BODY,{"disambiguationData":[OSD([sQuery(id+"F32.wireOp",EDGE,"E18"),sQuery(id+"F32.wireOp",EDGE,"E19"),sQuery(id+"F32.wireOp",EDGE,"E20"),sQuery(id+"F32.wireOp",EDGE,"E21"),sQuery(id+"F32.wireOp",EDGE,"E22"),sQuery(id+"F32.wireOp",EDGE,"E23")])]});
            transform(context, id + "F34", {"entities" : qUnion([Q0]), "transformType" : TransformType.TRANSLATION_3D, "dx" : 0 * mm, "dy" : 5 * mm, "dz" : 0 * mm, "makeCopy" : false});
        }
        {
            var Q0;
            Q0=makeQuery(id+"F33.opExtrude","SWEPT_BODY",BODY,{"disambiguationData":[OSD([sQuery(id+"F32.wireOp",EDGE,"E18"),sQuery(id+"F32.wireOp",EDGE,"E19"),sQuery(id+"F32.wireOp",EDGE,"E20"),sQuery(id+"F32.wireOp",EDGE,"E21"),sQuery(id+"F32.wireOp",EDGE,"E22"),sQuery(id+"F32.wireOp",EDGE,"E23")])]});
            var Q1;
            Q1=makeQuery(id+"F1.opExtrude","SWEPT_BODY",BODY,{"disambiguationData":[OSD([sQuery(id+"F0.wireOp",EDGE,"E2.bottom"),sQuery(id+"F0.wireOp",EDGE,"E2.top"),sQuery(id+"F0.wireOp",EDGE,"E2.left"),sQuery(id+"F0.wireOp",EDGE,"E2.right")])]});
            booleanBodies(context, id + "F35", {"operationType" : BooleanOperationType.SUBTRACTION, "tools" : qUnion([Q0]), "targets" : qUnion([Q1])});
        }
        {
            var Q0;
            Q0=makeQuery(id+"F5.opExtrude","SWEPT_BODY",BODY,{"disambiguationData":[OSD([sQuery(id+"F4.wireOp",EDGE,"E5"),sQuery(id+"F4.wireOp",EDGE,"E6"),sQuery(id+"F4.wireOp",EDGE,"E7"),sQuery(id+"F4.wireOp",EDGE,"E8"),sQuery(id+"F4.wireOp",EDGE,"E9")])]});
            deleteBodies(context, id + "F36", {"entities" : qUnion([Q0])});
        }
    });
